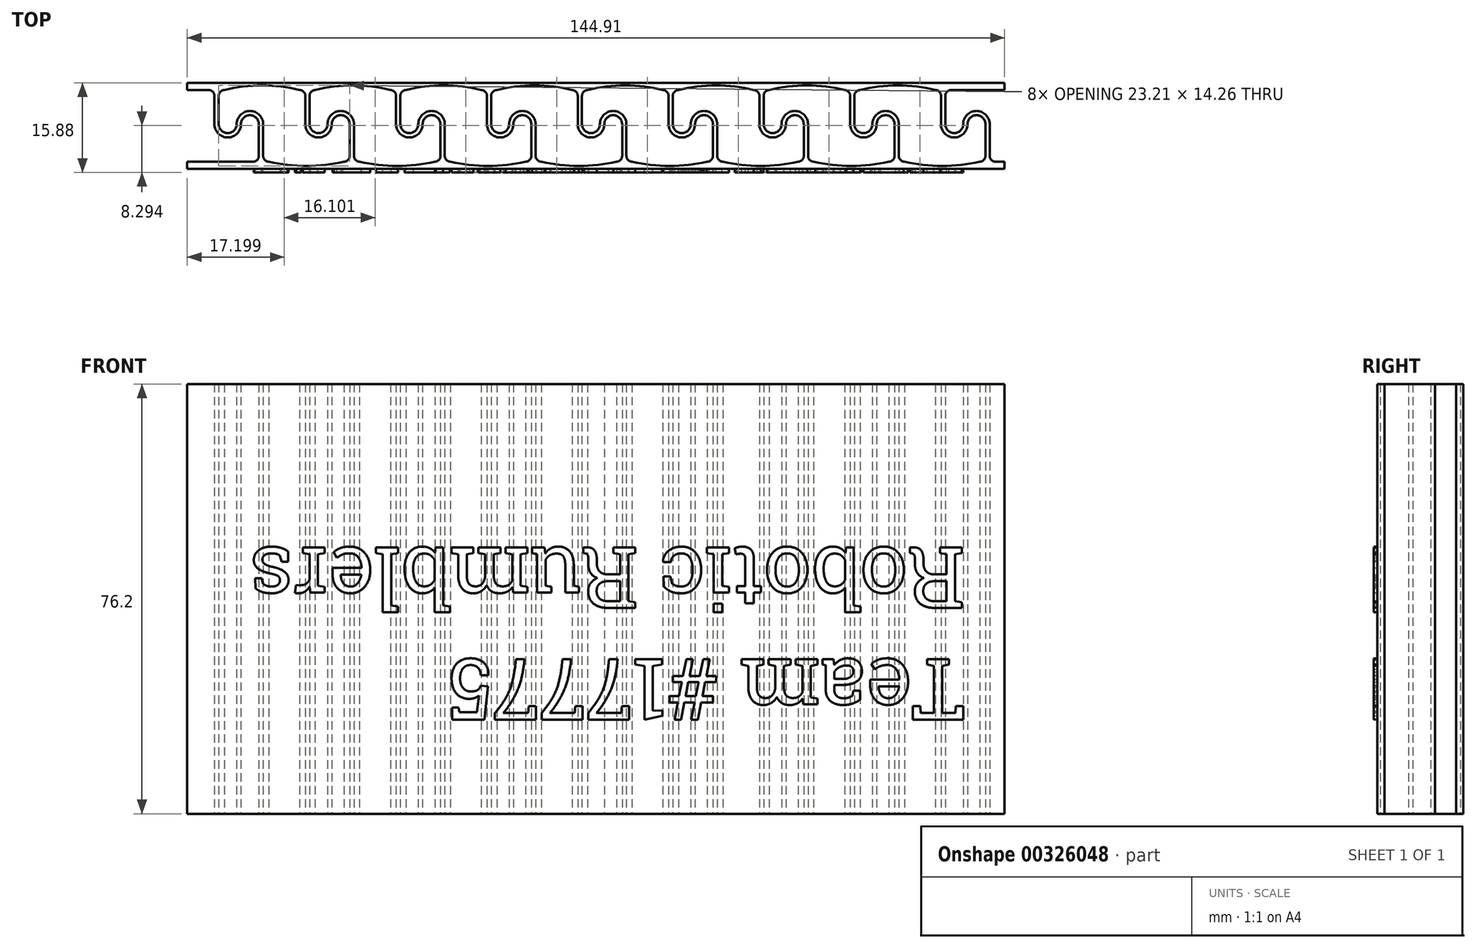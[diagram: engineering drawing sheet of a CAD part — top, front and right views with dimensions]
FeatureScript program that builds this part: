
annotation { "Feature Type Name" : "Feature", "Feature Type Description" : "" }
export const myFeature = defineFeature(function(context is Context, id is Id, definition is map)
    precondition{}
    {
        {
            var Q0;
            Q0=qCreatedBy(makeId("Front.planeOp"),FACE);
            var sketch = newSketch(context, id + "F0", { "sketchPlane" : qUnion([Q0])});
            skLineSegment(sketch, "E0", {"start": v(111.58, -16.44) * mm, "end": v(111.58, -17.71) * mm});
            skLineSegment(sketch, "E1", {"start": v(111.58, -17.71) * mm, "end": v(99.87, -17.71) * mm});
            skLineSegment(sketch, "E2", {"start": v(111.58, -30.41) * mm, "end": v(111.58, -31.68) * mm});
            skLineSegment(sketch, "E3", {"start": v(98.88, -18.7) * mm, "end": v(98.88, -24.35) * mm});
            skArc(sketch, "E4", {"start": v(98.88, -24.35) * mm, "mid": v(100.47, -25.94) * mm, "end": v(102.05, -24.35) * mm});
            skLineSegment(sketch, "E5", {"start": v(98.12, -18.7) * mm, "end": v(98.12, -24.35) * mm});
            skArc(sketch, "E6", {"start": v(98.12, -24.35) * mm, "mid": v(100.47, -26.7) * mm, "end": v(102.82, -24.35) * mm});
            skLineSegment(sketch, "E7", {"start": v(106, -29.42) * mm, "end": v(106, -24.35) * mm});
            skArc(sketch, "E8", {"start": v(106, -24.35) * mm, "mid": v(104.4, -22.77) * mm, "end": v(102.82, -24.35) * mm});
            skLineSegment(sketch, "E9", {"start": v(106.75, -29.42) * mm, "end": v(106.75, -24.35) * mm});
            skArc(sketch, "E10", {"start": v(106.75, -24.35) * mm, "mid": v(104.4, -22) * mm, "end": v(102.05, -24.35) * mm});
            skLineSegment(sketch, "E11", {"start": v(111.58, -30.41) * mm, "end": v(107.75, -30.41) * mm});
            skPoint(sketch, "E12.visualSharp", {"position": v(98.12, -17.71) * mm});
            skArc(sketch, "E12.filletArc", {"start": v(98.12, -18.7) * mm, "mid": v(97.83, -18) * mm, "end": v(97.13, -17.71) * mm});
            skPoint(sketch, "E13.visualSharp", {"position": v(98.88, -17.71) * mm});
            skArc(sketch, "E13.filletArc", {"start": v(99.87, -17.71) * mm, "mid": v(99.17, -18) * mm, "end": v(98.88, -18.7) * mm});
            skPoint(sketch, "E14.visualSharp", {"position": v(106, -30.41) * mm});
            skArc(sketch, "E14.filletArc", {"start": v(105, -30.41) * mm, "mid": v(105.7, -30.12) * mm, "end": v(106, -29.42) * mm});
            skPoint(sketch, "E15.visualSharp", {"position": v(106.75, -30.41) * mm});
            skArc(sketch, "E15.filletArc", {"start": v(106.75, -29.42) * mm, "mid": v(107.04, -30.12) * mm, "end": v(107.75, -30.41) * mm});
            skLineSegment(sketch, "E16", {"start": v(82.78, -18.7) * mm, "end": v(82.78, -24.35) * mm});
            skArc(sketch, "E17", {"start": v(82.78, -24.35) * mm, "mid": v(84.37, -25.94) * mm, "end": v(85.95, -24.35) * mm});
            skLineSegment(sketch, "E18", {"start": v(82.02, -18.7) * mm, "end": v(82.02, -24.35) * mm});
            skArc(sketch, "E19", {"start": v(82.02, -24.35) * mm, "mid": v(84.37, -26.7) * mm, "end": v(86.72, -24.35) * mm});
            skLineSegment(sketch, "E20", {"start": v(89.9, -29.42) * mm, "end": v(89.9, -24.35) * mm});
            skArc(sketch, "E21", {"start": v(89.9, -24.35) * mm, "mid": v(88.3, -22.77) * mm, "end": v(86.72, -24.35) * mm});
            skLineSegment(sketch, "E22", {"start": v(90.65, -29.42) * mm, "end": v(90.65, -24.35) * mm});
            skArc(sketch, "E23", {"start": v(90.65, -24.35) * mm, "mid": v(88.3, -22) * mm, "end": v(85.95, -24.35) * mm});
            skPoint(sketch, "E24.visualSharp", {"position": v(82.02, -17.71) * mm});
            skArc(sketch, "E24.filletArc", {"start": v(82.02, -18.7) * mm, "mid": v(81.73, -18) * mm, "end": v(81.02, -17.71) * mm});
            skPoint(sketch, "E25.visualSharp", {"position": v(82.78, -17.71) * mm});
            skArc(sketch, "E25.filletArc", {"start": v(83.77, -17.71) * mm, "mid": v(83.07, -18) * mm, "end": v(82.78, -18.7) * mm});
            skPoint(sketch, "E26.visualSharp", {"position": v(89.9, -30.41) * mm});
            skArc(sketch, "E26.filletArc", {"start": v(88.9, -30.41) * mm, "mid": v(89.6, -30.12) * mm, "end": v(89.9, -29.42) * mm});
            skPoint(sketch, "E27.visualSharp", {"position": v(90.65, -30.41) * mm});
            skArc(sketch, "E27.filletArc", {"start": v(90.65, -29.42) * mm, "mid": v(90.94, -30.12) * mm, "end": v(91.64, -30.41) * mm});
            skLineSegment(sketch, "E28", {"start": v(78.68, -17.71) * mm, "end": v(67.67, -17.71) * mm});
            skLineSegment(sketch, "E29", {"start": v(66.68, -18.7) * mm, "end": v(66.68, -24.35) * mm});
            skArc(sketch, "E30", {"start": v(66.68, -24.35) * mm, "mid": v(68.27, -25.94) * mm, "end": v(69.85, -24.35) * mm});
            skLineSegment(sketch, "E31", {"start": v(65.92, -18.7) * mm, "end": v(65.92, -24.35) * mm});
            skArc(sketch, "E32", {"start": v(65.92, -24.35) * mm, "mid": v(68.27, -26.7) * mm, "end": v(70.61, -24.35) * mm});
            skLineSegment(sketch, "E33", {"start": v(73.79, -29.42) * mm, "end": v(73.79, -24.35) * mm});
            skArc(sketch, "E34", {"start": v(73.79, -24.35) * mm, "mid": v(72.2, -22.77) * mm, "end": v(70.61, -24.35) * mm});
            skLineSegment(sketch, "E35", {"start": v(74.55, -29.42) * mm, "end": v(74.55, -24.35) * mm});
            skArc(sketch, "E36", {"start": v(74.55, -24.35) * mm, "mid": v(72.2, -22) * mm, "end": v(69.85, -24.35) * mm});
            skPoint(sketch, "E37.visualSharp", {"position": v(65.92, -17.71) * mm});
            skArc(sketch, "E37.filletArc", {"start": v(65.92, -18.7) * mm, "mid": v(65.63, -18) * mm, "end": v(64.92, -17.71) * mm});
            skPoint(sketch, "E38.visualSharp", {"position": v(66.68, -17.71) * mm});
            skArc(sketch, "E38.filletArc", {"start": v(67.67, -17.71) * mm, "mid": v(66.97, -18) * mm, "end": v(66.68, -18.7) * mm});
            skPoint(sketch, "E39.visualSharp", {"position": v(73.79, -30.41) * mm});
            skArc(sketch, "E39.filletArc", {"start": v(72.8, -30.41) * mm, "mid": v(73.5, -30.12) * mm, "end": v(73.79, -29.42) * mm});
            skPoint(sketch, "E40.visualSharp", {"position": v(74.55, -30.41) * mm});
            skArc(sketch, "E40.filletArc", {"start": v(74.55, -29.42) * mm, "mid": v(74.84, -30.12) * mm, "end": v(75.54, -30.41) * mm});
            skLineSegment(sketch, "E41", {"start": v(50.58, -18.7) * mm, "end": v(50.58, -24.35) * mm});
            skArc(sketch, "E42", {"start": v(50.58, -24.35) * mm, "mid": v(52.16, -25.94) * mm, "end": v(53.75, -24.35) * mm});
            skLineSegment(sketch, "E43", {"start": v(49.82, -18.7) * mm, "end": v(49.82, -24.35) * mm});
            skArc(sketch, "E44", {"start": v(49.82, -24.35) * mm, "mid": v(52.16, -26.7) * mm, "end": v(54.51, -24.35) * mm});
            skLineSegment(sketch, "E45", {"start": v(57.69, -29.42) * mm, "end": v(57.69, -24.35) * mm});
            skArc(sketch, "E46", {"start": v(57.69, -24.35) * mm, "mid": v(56.1, -22.77) * mm, "end": v(54.51, -24.35) * mm});
            skLineSegment(sketch, "E47", {"start": v(58.45, -29.42) * mm, "end": v(58.45, -24.35) * mm});
            skArc(sketch, "E48", {"start": v(58.45, -24.35) * mm, "mid": v(56.1, -22) * mm, "end": v(53.75, -24.35) * mm});
            skPoint(sketch, "E49.visualSharp", {"position": v(49.82, -17.71) * mm});
            skArc(sketch, "E49.filletArc", {"start": v(49.82, -18.7) * mm, "mid": v(49.52, -18) * mm, "end": v(48.82, -17.71) * mm});
            skPoint(sketch, "E50.visualSharp", {"position": v(50.58, -17.71) * mm});
            skArc(sketch, "E50.filletArc", {"start": v(51.57, -17.71) * mm, "mid": v(50.87, -18) * mm, "end": v(50.58, -18.7) * mm});
            skPoint(sketch, "E51.visualSharp", {"position": v(57.69, -30.41) * mm});
            skArc(sketch, "E51.filletArc", {"start": v(56.7, -30.41) * mm, "mid": v(57.4, -30.12) * mm, "end": v(57.69, -29.42) * mm});
            skPoint(sketch, "E52.visualSharp", {"position": v(58.45, -30.41) * mm});
            skArc(sketch, "E52.filletArc", {"start": v(58.45, -29.42) * mm, "mid": v(58.74, -30.12) * mm, "end": v(59.44, -30.41) * mm});
            skLineSegment(sketch, "E53", {"start": v(34.48, -18.7) * mm, "end": v(34.48, -24.35) * mm});
            skArc(sketch, "E54", {"start": v(34.48, -24.35) * mm, "mid": v(36.06, -25.94) * mm, "end": v(37.65, -24.35) * mm});
            skLineSegment(sketch, "E55", {"start": v(33.71, -18.7) * mm, "end": v(33.71, -24.35) * mm});
            skArc(sketch, "E56", {"start": v(33.71, -24.35) * mm, "mid": v(36.06, -26.7) * mm, "end": v(38.41, -24.35) * mm});
            skLineSegment(sketch, "E57", {"start": v(41.59, -29.42) * mm, "end": v(41.59, -24.35) * mm});
            skArc(sketch, "E58", {"start": v(41.59, -24.35) * mm, "mid": v(40, -22.77) * mm, "end": v(38.41, -24.35) * mm});
            skLineSegment(sketch, "E59", {"start": v(42.35, -29.42) * mm, "end": v(42.35, -24.35) * mm});
            skArc(sketch, "E60", {"start": v(42.35, -24.35) * mm, "mid": v(40, -22) * mm, "end": v(37.65, -24.35) * mm});
            skPoint(sketch, "E61.visualSharp", {"position": v(33.71, -17.71) * mm});
            skArc(sketch, "E61.filletArc", {"start": v(33.71, -18.7) * mm, "mid": v(33.42, -18) * mm, "end": v(32.72, -17.71) * mm});
            skPoint(sketch, "E62.visualSharp", {"position": v(34.48, -17.71) * mm});
            skArc(sketch, "E62.filletArc", {"start": v(35.47, -17.71) * mm, "mid": v(34.77, -18) * mm, "end": v(34.48, -18.7) * mm});
            skPoint(sketch, "E63.visualSharp", {"position": v(41.59, -30.41) * mm});
            skArc(sketch, "E63.filletArc", {"start": v(40.6, -30.41) * mm, "mid": v(41.3, -30.12) * mm, "end": v(41.59, -29.42) * mm});
            skPoint(sketch, "E64.visualSharp", {"position": v(42.35, -30.41) * mm});
            skArc(sketch, "E64.filletArc", {"start": v(42.35, -29.42) * mm, "mid": v(42.64, -30.12) * mm, "end": v(43.34, -30.41) * mm});
            skLineSegment(sketch, "E65", {"start": v(18.38, -18.7) * mm, "end": v(18.38, -24.35) * mm});
            skArc(sketch, "E66", {"start": v(18.38, -24.35) * mm, "mid": v(19.96, -25.94) * mm, "end": v(21.55, -24.35) * mm});
            skLineSegment(sketch, "E67", {"start": v(17.61, -18.7) * mm, "end": v(17.61, -24.35) * mm});
            skArc(sketch, "E68", {"start": v(17.61, -24.35) * mm, "mid": v(19.96, -26.7) * mm, "end": v(22.31, -24.35) * mm});
            skLineSegment(sketch, "E69", {"start": v(25.49, -29.42) * mm, "end": v(25.49, -24.35) * mm});
            skArc(sketch, "E70", {"start": v(25.49, -24.35) * mm, "mid": v(23.9, -22.77) * mm, "end": v(22.31, -24.35) * mm});
            skLineSegment(sketch, "E71", {"start": v(26.25, -29.42) * mm, "end": v(26.25, -24.35) * mm});
            skArc(sketch, "E72", {"start": v(26.25, -24.35) * mm, "mid": v(23.9, -22) * mm, "end": v(21.55, -24.35) * mm});
            skPoint(sketch, "E73.visualSharp", {"position": v(17.61, -17.71) * mm});
            skArc(sketch, "E73.filletArc", {"start": v(17.61, -18.7) * mm, "mid": v(17.32, -18) * mm, "end": v(16.62, -17.71) * mm});
            skPoint(sketch, "E74.visualSharp", {"position": v(18.38, -17.71) * mm});
            skArc(sketch, "E74.filletArc", {"start": v(19.37, -17.71) * mm, "mid": v(18.67, -18) * mm, "end": v(18.38, -18.7) * mm});
            skPoint(sketch, "E75.visualSharp", {"position": v(25.49, -30.41) * mm});
            skArc(sketch, "E75.filletArc", {"start": v(24.5, -30.41) * mm, "mid": v(25.2, -30.12) * mm, "end": v(25.49, -29.42) * mm});
            skPoint(sketch, "E76.visualSharp", {"position": v(26.25, -30.41) * mm});
            skArc(sketch, "E76.filletArc", {"start": v(26.25, -29.42) * mm, "mid": v(26.54, -30.12) * mm, "end": v(27.24, -30.41) * mm});
            skLineSegment(sketch, "E77", {"start": v(2.27, -18.7) * mm, "end": v(2.27, -24.35) * mm});
            skArc(sketch, "E78", {"start": v(2.27, -24.35) * mm, "mid": v(3.86, -25.94) * mm, "end": v(5.45, -24.35) * mm});
            skLineSegment(sketch, "E79", {"start": v(1.51, -18.7) * mm, "end": v(1.51, -24.35) * mm});
            skArc(sketch, "E80", {"start": v(1.51, -24.35) * mm, "mid": v(3.86, -26.7) * mm, "end": v(6.21, -24.35) * mm});
            skLineSegment(sketch, "E81", {"start": v(9.39, -29.42) * mm, "end": v(9.39, -24.35) * mm});
            skArc(sketch, "E82", {"start": v(9.39, -24.35) * mm, "mid": v(7.8, -22.77) * mm, "end": v(6.21, -24.35) * mm});
            skLineSegment(sketch, "E83", {"start": v(10.15, -29.42) * mm, "end": v(10.15, -24.35) * mm});
            skArc(sketch, "E84", {"start": v(10.15, -24.35) * mm, "mid": v(7.8, -22) * mm, "end": v(5.45, -24.35) * mm});
            skPoint(sketch, "E85.visualSharp", {"position": v(1.51, -17.71) * mm});
            skArc(sketch, "E85.filletArc", {"start": v(1.51, -18.7) * mm, "mid": v(1.22, -18) * mm, "end": v(0.52, -17.71) * mm});
            skPoint(sketch, "E86.visualSharp", {"position": v(2.27, -17.71) * mm});
            skArc(sketch, "E86.filletArc", {"start": v(3.27, -17.71) * mm, "mid": v(2.57, -18) * mm, "end": v(2.27, -18.7) * mm});
            skPoint(sketch, "E87.visualSharp", {"position": v(9.39, -30.41) * mm});
            skArc(sketch, "E87.filletArc", {"start": v(8.4, -30.41) * mm, "mid": v(9.1, -30.12) * mm, "end": v(9.39, -29.42) * mm});
            skPoint(sketch, "E88.visualSharp", {"position": v(10.15, -30.41) * mm});
            skArc(sketch, "E88.filletArc", {"start": v(10.15, -29.42) * mm, "mid": v(10.44, -30.12) * mm, "end": v(11.14, -30.41) * mm});
            skLineSegment(sketch, "E89", {"start": v(-13.83, -18.7) * mm, "end": v(-13.83, -24.35) * mm});
            skArc(sketch, "E90", {"start": v(-13.83, -24.35) * mm, "mid": v(-12.24, -25.94) * mm, "end": v(-10.65, -24.35) * mm});
            skLineSegment(sketch, "E91", {"start": v(-14.59, -18.7) * mm, "end": v(-14.59, -24.35) * mm});
            skArc(sketch, "E92", {"start": v(-14.59, -24.35) * mm, "mid": v(-12.24, -26.7) * mm, "end": v(-9.89, -24.35) * mm});
            skLineSegment(sketch, "E93", {"start": v(-6.71, -29.42) * mm, "end": v(-6.71, -24.35) * mm});
            skArc(sketch, "E94", {"start": v(-6.71, -24.35) * mm, "mid": v(-8.3, -22.77) * mm, "end": v(-9.89, -24.35) * mm});
            skLineSegment(sketch, "E95", {"start": v(-5.95, -29.42) * mm, "end": v(-5.95, -24.35) * mm});
            skArc(sketch, "E96", {"start": v(-5.95, -24.35) * mm, "mid": v(-8.3, -22) * mm, "end": v(-10.65, -24.35) * mm});
            skPoint(sketch, "E97.visualSharp", {"position": v(-14.59, -17.71) * mm});
            skArc(sketch, "E97.filletArc", {"start": v(-14.59, -18.7) * mm, "mid": v(-14.88, -18) * mm, "end": v(-15.58, -17.71) * mm});
            skPoint(sketch, "E98.visualSharp", {"position": v(-13.83, -17.71) * mm});
            skArc(sketch, "E98.filletArc", {"start": v(-12.83, -17.71) * mm, "mid": v(-13.54, -18) * mm, "end": v(-13.83, -18.7) * mm});
            skPoint(sketch, "E99.visualSharp", {"position": v(-6.71, -30.41) * mm});
            skArc(sketch, "E99.filletArc", {"start": v(-7.7, -30.41) * mm, "mid": v(-7, -30.12) * mm, "end": v(-6.71, -29.42) * mm});
            skPoint(sketch, "E100.visualSharp", {"position": v(-5.95, -30.41) * mm});
            skArc(sketch, "E100.filletArc", {"start": v(-5.95, -29.42) * mm, "mid": v(-5.66, -30.12) * mm, "end": v(-4.96, -30.41) * mm});
            skLineSegment(sketch, "E101", {"start": v(-29.93, -18.7) * mm, "end": v(-29.93, -24.35) * mm});
            skArc(sketch, "E102", {"start": v(-29.93, -24.35) * mm, "mid": v(-28.34, -25.94) * mm, "end": v(-26.75, -24.35) * mm});
            skLineSegment(sketch, "E103", {"start": v(-30.69, -18.7) * mm, "end": v(-30.69, -24.35) * mm});
            skArc(sketch, "E104", {"start": v(-30.69, -24.35) * mm, "mid": v(-28.34, -26.7) * mm, "end": v(-25.99, -24.35) * mm});
            skLineSegment(sketch, "E105", {"start": v(-22.81, -29.42) * mm, "end": v(-22.81, -24.35) * mm});
            skArc(sketch, "E106", {"start": v(-22.81, -24.35) * mm, "mid": v(-24.4, -22.77) * mm, "end": v(-25.99, -24.35) * mm});
            skLineSegment(sketch, "E107", {"start": v(-22.05, -29.42) * mm, "end": v(-22.05, -24.35) * mm});
            skArc(sketch, "E108", {"start": v(-22.05, -24.35) * mm, "mid": v(-24.4, -22) * mm, "end": v(-26.75, -24.35) * mm});
            skLineSegment(sketch, "E109", {"start": v(-31.68, -17.71) * mm, "end": v(-33.32, -17.71) * mm});
            skLineSegment(sketch, "E110", {"start": v(-23.8, -30.41) * mm, "end": v(-33.32, -30.41) * mm});
            skPoint(sketch, "E111.visualSharp", {"position": v(-30.69, -17.71) * mm});
            skArc(sketch, "E111.filletArc", {"start": v(-30.69, -18.7) * mm, "mid": v(-30.98, -18) * mm, "end": v(-31.68, -17.71) * mm});
            skPoint(sketch, "E112.visualSharp", {"position": v(-29.93, -17.71) * mm});
            skArc(sketch, "E112.filletArc", {"start": v(-28.93, -17.71) * mm, "mid": v(-29.64, -18) * mm, "end": v(-29.93, -18.7) * mm});
            skPoint(sketch, "E113.visualSharp", {"position": v(-22.81, -30.41) * mm});
            skArc(sketch, "E113.filletArc", {"start": v(-23.8, -30.41) * mm, "mid": v(-23.1, -30.12) * mm, "end": v(-22.81, -29.42) * mm});
            skPoint(sketch, "E114.visualSharp", {"position": v(-22.05, -30.41) * mm});
            skArc(sketch, "E114.filletArc", {"start": v(-22.05, -29.42) * mm, "mid": v(-21.76, -30.12) * mm, "end": v(-21.06, -30.41) * mm});
            skLineSegment(sketch, "E115", {"start": v(111.58, -16.44) * mm, "end": v(-33.32, -16.44) * mm});
            skLineSegment(sketch, "E116", {"start": v(-33.32, -16.44) * mm, "end": v(-33.32, -17.71) * mm});
            skLineSegment(sketch, "E117", {"start": v(111.58, -31.68) * mm, "end": v(-33.32, -31.68) * mm});
            skLineSegment(sketch, "E118", {"start": v(-33.32, -31.68) * mm, "end": v(-33.32, -30.41) * mm});
            skArc(sketch, "E119", {"start": v(-15.58, -17.71) * mm, "mid": v(-22.26, -16.96) * mm, "end": v(-28.93, -17.71) * mm});
            skArc(sketch, "E120", {"start": v(-21.06, -30.41) * mm, "mid": v(-14.38, -31.22) * mm, "end": v(-7.7, -30.41) * mm});
            skArc(sketch, "E121", {"start": v(-4.96, -30.41) * mm, "mid": v(1.72, -31.22) * mm, "end": v(8.4, -30.41) * mm});
            skArc(sketch, "E122", {"start": v(0.52, -17.71) * mm, "mid": v(-6.16, -16.96) * mm, "end": v(-12.83, -17.71) * mm});
            skArc(sketch, "E123", {"start": v(16.62, -17.71) * mm, "mid": v(9.94, -16.96) * mm, "end": v(3.27, -17.71) * mm});
            skArc(sketch, "E124", {"start": v(32.72, -17.71) * mm, "mid": v(26.05, -16.96) * mm, "end": v(19.37, -17.71) * mm});
            skArc(sketch, "E125", {"start": v(11.14, -30.41) * mm, "mid": v(17.82, -31.22) * mm, "end": v(24.5, -30.41) * mm});
            skArc(sketch, "E126", {"start": v(27.24, -30.41) * mm, "mid": v(33.92, -31.22) * mm, "end": v(40.6, -30.41) * mm});
            skArc(sketch, "E127", {"start": v(43.34, -30.41) * mm, "mid": v(50.02, -31.22) * mm, "end": v(56.7, -30.41) * mm});
            skArc(sketch, "E128", {"start": v(59.44, -30.41) * mm, "mid": v(66.12, -31.22) * mm, "end": v(72.8, -30.41) * mm});
            skArc(sketch, "E129", {"start": v(75.54, -30.41) * mm, "mid": v(82.22, -31.22) * mm, "end": v(88.9, -30.41) * mm});
            skArc(sketch, "E130", {"start": v(91.64, -30.41) * mm, "mid": v(98.32, -31.22) * mm, "end": v(105, -30.41) * mm});
            skArc(sketch, "E131", {"start": v(48.82, -17.71) * mm, "mid": v(42.15, -16.96) * mm, "end": v(35.47, -17.71) * mm});
            skArc(sketch, "E132", {"start": v(64.92, -17.71) * mm, "mid": v(58.25, -16.96) * mm, "end": v(51.57, -17.71) * mm});
            skArc(sketch, "E133", {"start": v(81.02, -17.71) * mm, "mid": v(74.35, -16.96) * mm, "end": v(67.67, -17.71) * mm});
            skArc(sketch, "E134", {"start": v(97.13, -17.71) * mm, "mid": v(90.45, -16.96) * mm, "end": v(83.77, -17.71) * mm});
            skSolve(sketch);
        }
        {
            var Q0;
            Q0=makeQuery(id+"F0.imprint","IMPRINT",FACE,{"disambiguationData":[TD([[makeQuery(id+"F0.imprint","IMPRINT",EDGE,{"derivedFrom":sQuery(id+"F0.wireOp",EDGE,"E0")}),-1.0]])]});
            extrude(context, id + "F1", {"entities" : qUnion([Q0]), "depth" : 76.2 * mm});
        }
        {
            var Q0;
            Q0=makeQuery(id+"F1.opExtrude","SWEPT_FACE",FACE,{"disambiguationData":[OSD([sQuery(id+"F0.wireOp",EDGE,"E115")])]});
            var sketch = newSketch(context, id + "F2", { "sketchPlane" : qUnion([Q0])});
            skText(sketch, "E135", { "text": "Team #17775\nRobotic Rumblers\n", "fontName": "RobotoSlab-Regular.ttf"});
            const initialGuessF2  = {"E135": [-0.02624, -0.02738, 1, 0, 0.0108]};
            skSetInitialGuess(sketch, initialGuessF2);
            skSolve(sketch);
        }
        {
            var Q0;
            Q0 = qSketchRegion(id + "F2", true);
            extrude(context, id + "F3", {"entities" : qUnion([Q0]), "operationType" : NewBodyOperationType.ADD, "depth" : 0.64 * mm, "hasDraft" : true, "draftAngle" : 3 * degree});
        }
        {
            var Q0;
            Q0=makeQuery(id+"F1.opExtrude","SWEPT_BODY",BODY,{"disambiguationData":[OSD([sQuery(id+"F0.wireOp",EDGE,"E0"),sQuery(id+"F0.wireOp",EDGE,"E1"),sQuery(id+"F0.wireOp",EDGE,"E2"),sQuery(id+"F0.wireOp",EDGE,"E3"),sQuery(id+"F0.wireOp",EDGE,"E4"),sQuery(id+"F0.wireOp",EDGE,"E5"),sQuery(id+"F0.wireOp",EDGE,"E6"),sQuery(id+"F0.wireOp",EDGE,"E7"),sQuery(id+"F0.wireOp",EDGE,"E8"),sQuery(id+"F0.wireOp",EDGE,"E9"),sQuery(id+"F0.wireOp",EDGE,"E10"),sQuery(id+"F0.wireOp",EDGE,"E11"),sQuery(id+"F0.wireOp",EDGE,"I74NB5Xt-fBUx-Ekq9-JF9C-fknuVL3scMMT"),sQuery(id+"F0.wireOp",EDGE,"4FDFUyAs-k7MS-Wikd-iGz1-CcvRFR4CWyGl"),sQuery(id+"F0.wireOp",EDGE,"E12.filletArc"),sQuery(id+"F0.wireOp",EDGE,"E13.filletArc"),sQuery(id+"F0.wireOp",EDGE,"E14.filletArc"),sQuery(id+"F0.wireOp",EDGE,"E15.filletArc"),sQuery(id+"F0.wireOp",EDGE,"a3bf5448-02e8-47db-9d06-bfbd453e25e5"),sQuery(id+"F0.wireOp",EDGE,"E16"),sQuery(id+"F0.wireOp",EDGE,"E17"),sQuery(id+"F0.wireOp",EDGE,"E18"),sQuery(id+"F0.wireOp",EDGE,"E19"),sQuery(id+"F0.wireOp",EDGE,"E20"),sQuery(id+"F0.wireOp",EDGE,"E21"),sQuery(id+"F0.wireOp",EDGE,"E22"),sQuery(id+"F0.wireOp",EDGE,"E23"),sQuery(id+"F0.wireOp",EDGE,"2c05487f-aafa-4f7c-aa8f-dc711a0f5cb2"),sQuery(id+"F0.wireOp",EDGE,"aa923bbd-f832-4f58-9164-6b3256058c8c"),sQuery(id+"F0.wireOp",EDGE,"d95c7900-678d-4411-9ef4-11f17a881cd2"),sQuery(id+"F0.wireOp",EDGE,"E24.filletArc"),sQuery(id+"F0.wireOp",EDGE,"E25.filletArc"),sQuery(id+"F0.wireOp",EDGE,"E26.filletArc"),sQuery(id+"F0.wireOp",EDGE,"E27.filletArc"),sQuery(id+"F0.wireOp",EDGE,"E28"),sQuery(id+"F0.wireOp",EDGE,"E29"),sQuery(id+"F0.wireOp",EDGE,"E30"),sQuery(id+"F0.wireOp",EDGE,"E31"),sQuery(id+"F0.wireOp",EDGE,"E32"),sQuery(id+"F0.wireOp",EDGE,"E33"),sQuery(id+"F0.wireOp",EDGE,"E34"),sQuery(id+"F0.wireOp",EDGE,"E35"),sQuery(id+"F0.wireOp",EDGE,"E36"),sQuery(id+"F0.wireOp",EDGE,"7487c359-1d13-442e-8d40-6b6f0a60b528"),sQuery(id+"F0.wireOp",EDGE,"0d321a95-f0bf-4603-844a-9d89d9bece21"),sQuery(id+"F0.wireOp",EDGE,"0b63d352-fbcd-48db-a107-9c6472e04aa2"),sQuery(id+"F0.wireOp",EDGE,"E37.filletArc"),sQuery(id+"F0.wireOp",EDGE,"E38.filletArc"),sQuery(id+"F0.wireOp",EDGE,"E39.filletArc"),sQuery(id+"F0.wireOp",EDGE,"E40.filletArc"),sQuery(id+"F0.wireOp",EDGE,"67e7e0cc-1dbd-4a8f-987f-19f6fc1f17c7"),sQuery(id+"F0.wireOp",EDGE,"E41"),sQuery(id+"F0.wireOp",EDGE,"E42"),sQuery(id+"F0.wireOp",EDGE,"E43"),sQuery(id+"F0.wireOp",EDGE,"E44"),sQuery(id+"F0.wireOp",EDGE,"E45"),sQuery(id+"F0.wireOp",EDGE,"E46"),sQuery(id+"F0.wireOp",EDGE,"E47"),sQuery(id+"F0.wireOp",EDGE,"E48"),sQuery(id+"F0.wireOp",EDGE,"d55768ac-2e07-4581-96c8-90a235a94c6e"),sQuery(id+"F0.wireOp",EDGE,"d56cd83a-e035-431e-9127-d553bba9e061"),sQuery(id+"F0.wireOp",EDGE,"8d056239-58ce-4037-b7b6-6b57657910ae"),sQuery(id+"F0.wireOp",EDGE,"E49.filletArc"),sQuery(id+"F0.wireOp",EDGE,"E50.filletArc"),sQuery(id+"F0.wireOp",EDGE,"E51.filletArc"),sQuery(id+"F0.wireOp",EDGE,"E52.filletArc"),sQuery(id+"F0.wireOp",EDGE,"689b71ce-addc-4fa1-bc7e-e4df8c8ebdf9"),sQuery(id+"F0.wireOp",EDGE,"E53"),sQuery(id+"F0.wireOp",EDGE,"E54"),sQuery(id+"F0.wireOp",EDGE,"E55"),sQuery(id+"F0.wireOp",EDGE,"E56"),sQuery(id+"F0.wireOp",EDGE,"E57"),sQuery(id+"F0.wireOp",EDGE,"E58"),sQuery(id+"F0.wireOp",EDGE,"E59"),sQuery(id+"F0.wireOp",EDGE,"E60"),sQuery(id+"F0.wireOp",EDGE,"0f5e8a53-58f9-4088-94ab-621361dd0740"),sQuery(id+"F0.wireOp",EDGE,"c80b85d9-e73a-4eb2-b9b9-34d3dfa9f6f2"),sQuery(id+"F0.wireOp",EDGE,"70b4659f-ba04-44f8-9531-555b2133b5da"),sQuery(id+"F0.wireOp",EDGE,"E61.filletArc"),sQuery(id+"F0.wireOp",EDGE,"E62.filletArc"),sQuery(id+"F0.wireOp",EDGE,"E63.filletArc"),sQuery(id+"F0.wireOp",EDGE,"E64.filletArc"),sQuery(id+"F0.wireOp",EDGE,"30e6c9bc-ddc1-4fb0-937a-8d0deabf5910"),sQuery(id+"F0.wireOp",EDGE,"E65"),sQuery(id+"F0.wireOp",EDGE,"E66"),sQuery(id+"F0.wireOp",EDGE,"E67"),sQuery(id+"F0.wireOp",EDGE,"E68"),sQuery(id+"F0.wireOp",EDGE,"E69"),sQuery(id+"F0.wireOp",EDGE,"E70"),sQuery(id+"F0.wireOp",EDGE,"E71"),sQuery(id+"F0.wireOp",EDGE,"E72"),sQuery(id+"F0.wireOp",EDGE,"8f9fa5c3-c251-432c-b5cf-c271094e8503"),sQuery(id+"F0.wireOp",EDGE,"48fe9f69-4303-4a16-b855-5b18747e6bbd"),sQuery(id+"F0.wireOp",EDGE,"adddb319-75e6-4134-aa0c-543cc49d29cf"),sQuery(id+"F0.wireOp",EDGE,"E73.filletArc"),sQuery(id+"F0.wireOp",EDGE,"E74.filletArc"),sQuery(id+"F0.wireOp",EDGE,"E75.filletArc"),sQuery(id+"F0.wireOp",EDGE,"E76.filletArc"),sQuery(id+"F0.wireOp",EDGE,"794929a8-fd93-45ab-9b8a-a8aae1a8e309"),sQuery(id+"F0.wireOp",EDGE,"E77"),sQuery(id+"F0.wireOp",EDGE,"E78"),sQuery(id+"F0.wireOp",EDGE,"E79"),sQuery(id+"F0.wireOp",EDGE,"E80"),sQuery(id+"F0.wireOp",EDGE,"E81"),sQuery(id+"F0.wireOp",EDGE,"E82"),sQuery(id+"F0.wireOp",EDGE,"E83"),sQuery(id+"F0.wireOp",EDGE,"E84"),sQuery(id+"F0.wireOp",EDGE,"c2507384-40c0-4369-9541-7014aa20dc06"),sQuery(id+"F0.wireOp",EDGE,"1daf244b-b26d-4da6-aa17-2b1b48277eff"),sQuery(id+"F0.wireOp",EDGE,"f3f5064b-9514-43f3-86fe-7d8dfe96d7c0"),sQuery(id+"F0.wireOp",EDGE,"E85.filletArc"),sQuery(id+"F0.wireOp",EDGE,"E86.filletArc"),sQuery(id+"F0.wireOp",EDGE,"E87.filletArc"),sQuery(id+"F0.wireOp",EDGE,"E88.filletArc"),sQuery(id+"F0.wireOp",EDGE,"db05fb30-ff1c-46d8-ad61-f310132a52e9"),sQuery(id+"F0.wireOp",EDGE,"E89"),sQuery(id+"F0.wireOp",EDGE,"E90"),sQuery(id+"F0.wireOp",EDGE,"E91"),sQuery(id+"F0.wireOp",EDGE,"E92"),sQuery(id+"F0.wireOp",EDGE,"E93"),sQuery(id+"F0.wireOp",EDGE,"E94"),sQuery(id+"F0.wireOp",EDGE,"E95"),sQuery(id+"F0.wireOp",EDGE,"E96"),sQuery(id+"F0.wireOp",EDGE,"1130a4e5-352a-40db-811d-9c2f480c6459"),sQuery(id+"F0.wireOp",EDGE,"eab22e00-a051-4c91-887e-3bb937c10980"),sQuery(id+"F0.wireOp",EDGE,"d1e682f2-d9a5-40f1-908d-0a2fb979e1ca"),sQuery(id+"F0.wireOp",EDGE,"E97.filletArc"),sQuery(id+"F0.wireOp",EDGE,"E98.filletArc"),sQuery(id+"F0.wireOp",EDGE,"E99.filletArc"),sQuery(id+"F0.wireOp",EDGE,"E100.filletArc"),sQuery(id+"F0.wireOp",EDGE,"e89af864-c7d1-4349-afac-df63decef93c"),sQuery(id+"F0.wireOp",EDGE,"E101"),sQuery(id+"F0.wireOp",EDGE,"E102"),sQuery(id+"F0.wireOp",EDGE,"E103"),sQuery(id+"F0.wireOp",EDGE,"E104"),sQuery(id+"F0.wireOp",EDGE,"E105"),sQuery(id+"F0.wireOp",EDGE,"E106"),sQuery(id+"F0.wireOp",EDGE,"E107"),sQuery(id+"F0.wireOp",EDGE,"E108"),sQuery(id+"F0.wireOp",EDGE,"23fffc08-2727-465d-9e6f-753851ddf39a"),sQuery(id+"F0.wireOp",EDGE,"E109"),sQuery(id+"F0.wireOp",EDGE,"E110"),sQuery(id+"F0.wireOp",EDGE,"E111.filletArc"),sQuery(id+"F0.wireOp",EDGE,"E112.filletArc"),sQuery(id+"F0.wireOp",EDGE,"E113.filletArc"),sQuery(id+"F0.wireOp",EDGE,"E114.filletArc"),sQuery(id+"F0.wireOp",EDGE,"E115"),sQuery(id+"F0.wireOp",EDGE,"E116"),sQuery(id+"F0.wireOp",EDGE,"E117"),sQuery(id+"F0.wireOp",EDGE,"E118")])]});
            var Q1;
            Q1=makeQuery(id+"F1.opExtrude","CAP_VERTEX",VERTEX,{"disambiguationData":[OSD([sQuery(id+"F0.wireOp",EDGE,"E117"),sQuery(id+"F0.wireOp",EDGE,"E118")])],"isStart":true});
            var Q2;
            Q2=qCreatedBy(makeId("Origin.pointOp"),VERTEX);
            transform(context, id + "F4", {"entities" : qUnion([Q0]), "transformType" : TransformType.TRANSLATION_ENTITY, "oppositeDirectionEntity" : false, "transformLine" : qUnion([Q1, Q2]), "makeCopy" : false});
        }
        {
            var Q0;
            Q0=makeQuery(id+"F1.opExtrude","SWEPT_BODY",BODY,{"disambiguationData":[OSD([sQuery(id+"F0.wireOp",EDGE,"E0"),sQuery(id+"F0.wireOp",EDGE,"E1"),sQuery(id+"F0.wireOp",EDGE,"E2"),sQuery(id+"F0.wireOp",EDGE,"E3"),sQuery(id+"F0.wireOp",EDGE,"E4"),sQuery(id+"F0.wireOp",EDGE,"E5"),sQuery(id+"F0.wireOp",EDGE,"E6"),sQuery(id+"F0.wireOp",EDGE,"E7"),sQuery(id+"F0.wireOp",EDGE,"E8"),sQuery(id+"F0.wireOp",EDGE,"E9"),sQuery(id+"F0.wireOp",EDGE,"E10"),sQuery(id+"F0.wireOp",EDGE,"E11"),sQuery(id+"F0.wireOp",EDGE,"I74NB5Xt-fBUx-Ekq9-JF9C-fknuVL3scMMT"),sQuery(id+"F0.wireOp",EDGE,"4FDFUyAs-k7MS-Wikd-iGz1-CcvRFR4CWyGl"),sQuery(id+"F0.wireOp",EDGE,"E12.filletArc"),sQuery(id+"F0.wireOp",EDGE,"E13.filletArc"),sQuery(id+"F0.wireOp",EDGE,"E14.filletArc"),sQuery(id+"F0.wireOp",EDGE,"E15.filletArc"),sQuery(id+"F0.wireOp",EDGE,"a3bf5448-02e8-47db-9d06-bfbd453e25e5"),sQuery(id+"F0.wireOp",EDGE,"E16"),sQuery(id+"F0.wireOp",EDGE,"E17"),sQuery(id+"F0.wireOp",EDGE,"E18"),sQuery(id+"F0.wireOp",EDGE,"E19"),sQuery(id+"F0.wireOp",EDGE,"E20"),sQuery(id+"F0.wireOp",EDGE,"E21"),sQuery(id+"F0.wireOp",EDGE,"E22"),sQuery(id+"F0.wireOp",EDGE,"E23"),sQuery(id+"F0.wireOp",EDGE,"2c05487f-aafa-4f7c-aa8f-dc711a0f5cb2"),sQuery(id+"F0.wireOp",EDGE,"aa923bbd-f832-4f58-9164-6b3256058c8c"),sQuery(id+"F0.wireOp",EDGE,"d95c7900-678d-4411-9ef4-11f17a881cd2"),sQuery(id+"F0.wireOp",EDGE,"E24.filletArc"),sQuery(id+"F0.wireOp",EDGE,"E25.filletArc"),sQuery(id+"F0.wireOp",EDGE,"E26.filletArc"),sQuery(id+"F0.wireOp",EDGE,"E27.filletArc"),sQuery(id+"F0.wireOp",EDGE,"E28"),sQuery(id+"F0.wireOp",EDGE,"E29"),sQuery(id+"F0.wireOp",EDGE,"E30"),sQuery(id+"F0.wireOp",EDGE,"E31"),sQuery(id+"F0.wireOp",EDGE,"E32"),sQuery(id+"F0.wireOp",EDGE,"E33"),sQuery(id+"F0.wireOp",EDGE,"E34"),sQuery(id+"F0.wireOp",EDGE,"E35"),sQuery(id+"F0.wireOp",EDGE,"E36"),sQuery(id+"F0.wireOp",EDGE,"7487c359-1d13-442e-8d40-6b6f0a60b528"),sQuery(id+"F0.wireOp",EDGE,"0d321a95-f0bf-4603-844a-9d89d9bece21"),sQuery(id+"F0.wireOp",EDGE,"0b63d352-fbcd-48db-a107-9c6472e04aa2"),sQuery(id+"F0.wireOp",EDGE,"E37.filletArc"),sQuery(id+"F0.wireOp",EDGE,"E38.filletArc"),sQuery(id+"F0.wireOp",EDGE,"E39.filletArc"),sQuery(id+"F0.wireOp",EDGE,"E40.filletArc"),sQuery(id+"F0.wireOp",EDGE,"67e7e0cc-1dbd-4a8f-987f-19f6fc1f17c7"),sQuery(id+"F0.wireOp",EDGE,"E41"),sQuery(id+"F0.wireOp",EDGE,"E42"),sQuery(id+"F0.wireOp",EDGE,"E43"),sQuery(id+"F0.wireOp",EDGE,"E44"),sQuery(id+"F0.wireOp",EDGE,"E45"),sQuery(id+"F0.wireOp",EDGE,"E46"),sQuery(id+"F0.wireOp",EDGE,"E47"),sQuery(id+"F0.wireOp",EDGE,"E48"),sQuery(id+"F0.wireOp",EDGE,"d55768ac-2e07-4581-96c8-90a235a94c6e"),sQuery(id+"F0.wireOp",EDGE,"d56cd83a-e035-431e-9127-d553bba9e061"),sQuery(id+"F0.wireOp",EDGE,"8d056239-58ce-4037-b7b6-6b57657910ae"),sQuery(id+"F0.wireOp",EDGE,"E49.filletArc"),sQuery(id+"F0.wireOp",EDGE,"E50.filletArc"),sQuery(id+"F0.wireOp",EDGE,"E51.filletArc"),sQuery(id+"F0.wireOp",EDGE,"E52.filletArc"),sQuery(id+"F0.wireOp",EDGE,"689b71ce-addc-4fa1-bc7e-e4df8c8ebdf9"),sQuery(id+"F0.wireOp",EDGE,"E53"),sQuery(id+"F0.wireOp",EDGE,"E54"),sQuery(id+"F0.wireOp",EDGE,"E55"),sQuery(id+"F0.wireOp",EDGE,"E56"),sQuery(id+"F0.wireOp",EDGE,"E57"),sQuery(id+"F0.wireOp",EDGE,"E58"),sQuery(id+"F0.wireOp",EDGE,"E59"),sQuery(id+"F0.wireOp",EDGE,"E60"),sQuery(id+"F0.wireOp",EDGE,"0f5e8a53-58f9-4088-94ab-621361dd0740"),sQuery(id+"F0.wireOp",EDGE,"c80b85d9-e73a-4eb2-b9b9-34d3dfa9f6f2"),sQuery(id+"F0.wireOp",EDGE,"70b4659f-ba04-44f8-9531-555b2133b5da"),sQuery(id+"F0.wireOp",EDGE,"E61.filletArc"),sQuery(id+"F0.wireOp",EDGE,"E62.filletArc"),sQuery(id+"F0.wireOp",EDGE,"E63.filletArc"),sQuery(id+"F0.wireOp",EDGE,"E64.filletArc"),sQuery(id+"F0.wireOp",EDGE,"30e6c9bc-ddc1-4fb0-937a-8d0deabf5910"),sQuery(id+"F0.wireOp",EDGE,"E65"),sQuery(id+"F0.wireOp",EDGE,"E66"),sQuery(id+"F0.wireOp",EDGE,"E67"),sQuery(id+"F0.wireOp",EDGE,"E68"),sQuery(id+"F0.wireOp",EDGE,"E69"),sQuery(id+"F0.wireOp",EDGE,"E70"),sQuery(id+"F0.wireOp",EDGE,"E71"),sQuery(id+"F0.wireOp",EDGE,"E72"),sQuery(id+"F0.wireOp",EDGE,"8f9fa5c3-c251-432c-b5cf-c271094e8503"),sQuery(id+"F0.wireOp",EDGE,"48fe9f69-4303-4a16-b855-5b18747e6bbd"),sQuery(id+"F0.wireOp",EDGE,"adddb319-75e6-4134-aa0c-543cc49d29cf"),sQuery(id+"F0.wireOp",EDGE,"E73.filletArc"),sQuery(id+"F0.wireOp",EDGE,"E74.filletArc"),sQuery(id+"F0.wireOp",EDGE,"E75.filletArc"),sQuery(id+"F0.wireOp",EDGE,"E76.filletArc"),sQuery(id+"F0.wireOp",EDGE,"794929a8-fd93-45ab-9b8a-a8aae1a8e309"),sQuery(id+"F0.wireOp",EDGE,"E77"),sQuery(id+"F0.wireOp",EDGE,"E78"),sQuery(id+"F0.wireOp",EDGE,"E79"),sQuery(id+"F0.wireOp",EDGE,"E80"),sQuery(id+"F0.wireOp",EDGE,"E81"),sQuery(id+"F0.wireOp",EDGE,"E82"),sQuery(id+"F0.wireOp",EDGE,"E83"),sQuery(id+"F0.wireOp",EDGE,"E84"),sQuery(id+"F0.wireOp",EDGE,"c2507384-40c0-4369-9541-7014aa20dc06"),sQuery(id+"F0.wireOp",EDGE,"1daf244b-b26d-4da6-aa17-2b1b48277eff"),sQuery(id+"F0.wireOp",EDGE,"f3f5064b-9514-43f3-86fe-7d8dfe96d7c0"),sQuery(id+"F0.wireOp",EDGE,"E85.filletArc"),sQuery(id+"F0.wireOp",EDGE,"E86.filletArc"),sQuery(id+"F0.wireOp",EDGE,"E87.filletArc"),sQuery(id+"F0.wireOp",EDGE,"E88.filletArc"),sQuery(id+"F0.wireOp",EDGE,"db05fb30-ff1c-46d8-ad61-f310132a52e9"),sQuery(id+"F0.wireOp",EDGE,"E89"),sQuery(id+"F0.wireOp",EDGE,"E90"),sQuery(id+"F0.wireOp",EDGE,"E91"),sQuery(id+"F0.wireOp",EDGE,"E92"),sQuery(id+"F0.wireOp",EDGE,"E93"),sQuery(id+"F0.wireOp",EDGE,"E94"),sQuery(id+"F0.wireOp",EDGE,"E95"),sQuery(id+"F0.wireOp",EDGE,"E96"),sQuery(id+"F0.wireOp",EDGE,"1130a4e5-352a-40db-811d-9c2f480c6459"),sQuery(id+"F0.wireOp",EDGE,"eab22e00-a051-4c91-887e-3bb937c10980"),sQuery(id+"F0.wireOp",EDGE,"d1e682f2-d9a5-40f1-908d-0a2fb979e1ca"),sQuery(id+"F0.wireOp",EDGE,"E97.filletArc"),sQuery(id+"F0.wireOp",EDGE,"E98.filletArc"),sQuery(id+"F0.wireOp",EDGE,"E99.filletArc"),sQuery(id+"F0.wireOp",EDGE,"E100.filletArc"),sQuery(id+"F0.wireOp",EDGE,"e89af864-c7d1-4349-afac-df63decef93c"),sQuery(id+"F0.wireOp",EDGE,"E101"),sQuery(id+"F0.wireOp",EDGE,"E102"),sQuery(id+"F0.wireOp",EDGE,"E103"),sQuery(id+"F0.wireOp",EDGE,"E104"),sQuery(id+"F0.wireOp",EDGE,"E105"),sQuery(id+"F0.wireOp",EDGE,"E106"),sQuery(id+"F0.wireOp",EDGE,"E107"),sQuery(id+"F0.wireOp",EDGE,"E108"),sQuery(id+"F0.wireOp",EDGE,"23fffc08-2727-465d-9e6f-753851ddf39a"),sQuery(id+"F0.wireOp",EDGE,"E109"),sQuery(id+"F0.wireOp",EDGE,"E110"),sQuery(id+"F0.wireOp",EDGE,"E111.filletArc"),sQuery(id+"F0.wireOp",EDGE,"E112.filletArc"),sQuery(id+"F0.wireOp",EDGE,"E113.filletArc"),sQuery(id+"F0.wireOp",EDGE,"E114.filletArc"),sQuery(id+"F0.wireOp",EDGE,"E115"),sQuery(id+"F0.wireOp",EDGE,"E116"),sQuery(id+"F0.wireOp",EDGE,"E117"),sQuery(id+"F0.wireOp",EDGE,"E118")])]});
            var Q1;
            Q1=makeQuery(id+"F1.opExtrude","CAP_EDGE",EDGE,{"disambiguationData":[OSD([sQuery(id+"F0.wireOp",EDGE,"E117")])],"isStart":true});
            transform(context, id + "F5", {"entities" : qUnion([Q0]), "transformType" : TransformType.ROTATION, "transformAxis" : qUnion([Q1]), "angle" : 90 * degree, "makeCopy" : false});
        }
        {
            var Q0;
            Q0=makeQuery(id+"F1.opExtrude","SWEPT_BODY",BODY,{"disambiguationData":[OSD([sQuery(id+"F0.wireOp",EDGE,"E0"),sQuery(id+"F0.wireOp",EDGE,"E1"),sQuery(id+"F0.wireOp",EDGE,"E2"),sQuery(id+"F0.wireOp",EDGE,"E3"),sQuery(id+"F0.wireOp",EDGE,"E4"),sQuery(id+"F0.wireOp",EDGE,"E5"),sQuery(id+"F0.wireOp",EDGE,"E6"),sQuery(id+"F0.wireOp",EDGE,"E7"),sQuery(id+"F0.wireOp",EDGE,"E8"),sQuery(id+"F0.wireOp",EDGE,"E9"),sQuery(id+"F0.wireOp",EDGE,"E10"),sQuery(id+"F0.wireOp",EDGE,"E11"),sQuery(id+"F0.wireOp",EDGE,"I74NB5Xt-fBUx-Ekq9-JF9C-fknuVL3scMMT"),sQuery(id+"F0.wireOp",EDGE,"4FDFUyAs-k7MS-Wikd-iGz1-CcvRFR4CWyGl"),sQuery(id+"F0.wireOp",EDGE,"E12.filletArc"),sQuery(id+"F0.wireOp",EDGE,"E13.filletArc"),sQuery(id+"F0.wireOp",EDGE,"E14.filletArc"),sQuery(id+"F0.wireOp",EDGE,"E15.filletArc"),sQuery(id+"F0.wireOp",EDGE,"a3bf5448-02e8-47db-9d06-bfbd453e25e5"),sQuery(id+"F0.wireOp",EDGE,"E16"),sQuery(id+"F0.wireOp",EDGE,"E17"),sQuery(id+"F0.wireOp",EDGE,"E18"),sQuery(id+"F0.wireOp",EDGE,"E19"),sQuery(id+"F0.wireOp",EDGE,"E20"),sQuery(id+"F0.wireOp",EDGE,"E21"),sQuery(id+"F0.wireOp",EDGE,"E22"),sQuery(id+"F0.wireOp",EDGE,"E23"),sQuery(id+"F0.wireOp",EDGE,"2c05487f-aafa-4f7c-aa8f-dc711a0f5cb2"),sQuery(id+"F0.wireOp",EDGE,"aa923bbd-f832-4f58-9164-6b3256058c8c"),sQuery(id+"F0.wireOp",EDGE,"d95c7900-678d-4411-9ef4-11f17a881cd2"),sQuery(id+"F0.wireOp",EDGE,"E24.filletArc"),sQuery(id+"F0.wireOp",EDGE,"E25.filletArc"),sQuery(id+"F0.wireOp",EDGE,"E26.filletArc"),sQuery(id+"F0.wireOp",EDGE,"E27.filletArc"),sQuery(id+"F0.wireOp",EDGE,"E28"),sQuery(id+"F0.wireOp",EDGE,"E29"),sQuery(id+"F0.wireOp",EDGE,"E30"),sQuery(id+"F0.wireOp",EDGE,"E31"),sQuery(id+"F0.wireOp",EDGE,"E32"),sQuery(id+"F0.wireOp",EDGE,"E33"),sQuery(id+"F0.wireOp",EDGE,"E34"),sQuery(id+"F0.wireOp",EDGE,"E35"),sQuery(id+"F0.wireOp",EDGE,"E36"),sQuery(id+"F0.wireOp",EDGE,"7487c359-1d13-442e-8d40-6b6f0a60b528"),sQuery(id+"F0.wireOp",EDGE,"0d321a95-f0bf-4603-844a-9d89d9bece21"),sQuery(id+"F0.wireOp",EDGE,"0b63d352-fbcd-48db-a107-9c6472e04aa2"),sQuery(id+"F0.wireOp",EDGE,"E37.filletArc"),sQuery(id+"F0.wireOp",EDGE,"E38.filletArc"),sQuery(id+"F0.wireOp",EDGE,"E39.filletArc"),sQuery(id+"F0.wireOp",EDGE,"E40.filletArc"),sQuery(id+"F0.wireOp",EDGE,"67e7e0cc-1dbd-4a8f-987f-19f6fc1f17c7"),sQuery(id+"F0.wireOp",EDGE,"E41"),sQuery(id+"F0.wireOp",EDGE,"E42"),sQuery(id+"F0.wireOp",EDGE,"E43"),sQuery(id+"F0.wireOp",EDGE,"E44"),sQuery(id+"F0.wireOp",EDGE,"E45"),sQuery(id+"F0.wireOp",EDGE,"E46"),sQuery(id+"F0.wireOp",EDGE,"E47"),sQuery(id+"F0.wireOp",EDGE,"E48"),sQuery(id+"F0.wireOp",EDGE,"d55768ac-2e07-4581-96c8-90a235a94c6e"),sQuery(id+"F0.wireOp",EDGE,"d56cd83a-e035-431e-9127-d553bba9e061"),sQuery(id+"F0.wireOp",EDGE,"8d056239-58ce-4037-b7b6-6b57657910ae"),sQuery(id+"F0.wireOp",EDGE,"E49.filletArc"),sQuery(id+"F0.wireOp",EDGE,"E50.filletArc"),sQuery(id+"F0.wireOp",EDGE,"E51.filletArc"),sQuery(id+"F0.wireOp",EDGE,"E52.filletArc"),sQuery(id+"F0.wireOp",EDGE,"689b71ce-addc-4fa1-bc7e-e4df8c8ebdf9"),sQuery(id+"F0.wireOp",EDGE,"E53"),sQuery(id+"F0.wireOp",EDGE,"E54"),sQuery(id+"F0.wireOp",EDGE,"E55"),sQuery(id+"F0.wireOp",EDGE,"E56"),sQuery(id+"F0.wireOp",EDGE,"E57"),sQuery(id+"F0.wireOp",EDGE,"E58"),sQuery(id+"F0.wireOp",EDGE,"E59"),sQuery(id+"F0.wireOp",EDGE,"E60"),sQuery(id+"F0.wireOp",EDGE,"0f5e8a53-58f9-4088-94ab-621361dd0740"),sQuery(id+"F0.wireOp",EDGE,"c80b85d9-e73a-4eb2-b9b9-34d3dfa9f6f2"),sQuery(id+"F0.wireOp",EDGE,"70b4659f-ba04-44f8-9531-555b2133b5da"),sQuery(id+"F0.wireOp",EDGE,"E61.filletArc"),sQuery(id+"F0.wireOp",EDGE,"E62.filletArc"),sQuery(id+"F0.wireOp",EDGE,"E63.filletArc"),sQuery(id+"F0.wireOp",EDGE,"E64.filletArc"),sQuery(id+"F0.wireOp",EDGE,"30e6c9bc-ddc1-4fb0-937a-8d0deabf5910"),sQuery(id+"F0.wireOp",EDGE,"E65"),sQuery(id+"F0.wireOp",EDGE,"E66"),sQuery(id+"F0.wireOp",EDGE,"E67"),sQuery(id+"F0.wireOp",EDGE,"E68"),sQuery(id+"F0.wireOp",EDGE,"E69"),sQuery(id+"F0.wireOp",EDGE,"E70"),sQuery(id+"F0.wireOp",EDGE,"E71"),sQuery(id+"F0.wireOp",EDGE,"E72"),sQuery(id+"F0.wireOp",EDGE,"8f9fa5c3-c251-432c-b5cf-c271094e8503"),sQuery(id+"F0.wireOp",EDGE,"48fe9f69-4303-4a16-b855-5b18747e6bbd"),sQuery(id+"F0.wireOp",EDGE,"adddb319-75e6-4134-aa0c-543cc49d29cf"),sQuery(id+"F0.wireOp",EDGE,"E73.filletArc"),sQuery(id+"F0.wireOp",EDGE,"E74.filletArc"),sQuery(id+"F0.wireOp",EDGE,"E75.filletArc"),sQuery(id+"F0.wireOp",EDGE,"E76.filletArc"),sQuery(id+"F0.wireOp",EDGE,"794929a8-fd93-45ab-9b8a-a8aae1a8e309"),sQuery(id+"F0.wireOp",EDGE,"E77"),sQuery(id+"F0.wireOp",EDGE,"E78"),sQuery(id+"F0.wireOp",EDGE,"E79"),sQuery(id+"F0.wireOp",EDGE,"E80"),sQuery(id+"F0.wireOp",EDGE,"E81"),sQuery(id+"F0.wireOp",EDGE,"E82"),sQuery(id+"F0.wireOp",EDGE,"E83"),sQuery(id+"F0.wireOp",EDGE,"E84"),sQuery(id+"F0.wireOp",EDGE,"c2507384-40c0-4369-9541-7014aa20dc06"),sQuery(id+"F0.wireOp",EDGE,"1daf244b-b26d-4da6-aa17-2b1b48277eff"),sQuery(id+"F0.wireOp",EDGE,"f3f5064b-9514-43f3-86fe-7d8dfe96d7c0"),sQuery(id+"F0.wireOp",EDGE,"E85.filletArc"),sQuery(id+"F0.wireOp",EDGE,"E86.filletArc"),sQuery(id+"F0.wireOp",EDGE,"E87.filletArc"),sQuery(id+"F0.wireOp",EDGE,"E88.filletArc"),sQuery(id+"F0.wireOp",EDGE,"db05fb30-ff1c-46d8-ad61-f310132a52e9"),sQuery(id+"F0.wireOp",EDGE,"E89"),sQuery(id+"F0.wireOp",EDGE,"E90"),sQuery(id+"F0.wireOp",EDGE,"E91"),sQuery(id+"F0.wireOp",EDGE,"E92"),sQuery(id+"F0.wireOp",EDGE,"E93"),sQuery(id+"F0.wireOp",EDGE,"E94"),sQuery(id+"F0.wireOp",EDGE,"E95"),sQuery(id+"F0.wireOp",EDGE,"E96"),sQuery(id+"F0.wireOp",EDGE,"1130a4e5-352a-40db-811d-9c2f480c6459"),sQuery(id+"F0.wireOp",EDGE,"eab22e00-a051-4c91-887e-3bb937c10980"),sQuery(id+"F0.wireOp",EDGE,"d1e682f2-d9a5-40f1-908d-0a2fb979e1ca"),sQuery(id+"F0.wireOp",EDGE,"E97.filletArc"),sQuery(id+"F0.wireOp",EDGE,"E98.filletArc"),sQuery(id+"F0.wireOp",EDGE,"E99.filletArc"),sQuery(id+"F0.wireOp",EDGE,"E100.filletArc"),sQuery(id+"F0.wireOp",EDGE,"e89af864-c7d1-4349-afac-df63decef93c"),sQuery(id+"F0.wireOp",EDGE,"E101"),sQuery(id+"F0.wireOp",EDGE,"E102"),sQuery(id+"F0.wireOp",EDGE,"E103"),sQuery(id+"F0.wireOp",EDGE,"E104"),sQuery(id+"F0.wireOp",EDGE,"E105"),sQuery(id+"F0.wireOp",EDGE,"E106"),sQuery(id+"F0.wireOp",EDGE,"E107"),sQuery(id+"F0.wireOp",EDGE,"E108"),sQuery(id+"F0.wireOp",EDGE,"23fffc08-2727-465d-9e6f-753851ddf39a"),sQuery(id+"F0.wireOp",EDGE,"E109"),sQuery(id+"F0.wireOp",EDGE,"E110"),sQuery(id+"F0.wireOp",EDGE,"E111.filletArc"),sQuery(id+"F0.wireOp",EDGE,"E112.filletArc"),sQuery(id+"F0.wireOp",EDGE,"E113.filletArc"),sQuery(id+"F0.wireOp",EDGE,"E114.filletArc"),sQuery(id+"F0.wireOp",EDGE,"E115"),sQuery(id+"F0.wireOp",EDGE,"E116"),sQuery(id+"F0.wireOp",EDGE,"E117"),sQuery(id+"F0.wireOp",EDGE,"E118")])]});
            var Q1;
            Q1=makeQuery(id+"F1.opExtrude","SWEPT_EDGE",EDGE,{"disambiguationData":[OSD([sQuery(id+"F0.wireOp",EDGE,"E117"),sQuery(id+"F0.wireOp",EDGE,"E118")])]});
            transform(context, id + "F6", {"entities" : qUnion([Q0]), "transformType" : TransformType.ROTATION, "transformAxis" : qUnion([Q1]), "angle" : 180 * degree, "makeCopy" : false});
        }
        {
            var Q0;
            Q0=makeQuery(id+"F1.opExtrude","SWEPT_BODY",BODY,{"disambiguationData":[OSD([sQuery(id+"F0.wireOp",EDGE,"E0"),sQuery(id+"F0.wireOp",EDGE,"E1"),sQuery(id+"F0.wireOp",EDGE,"E2"),sQuery(id+"F0.wireOp",EDGE,"E3"),sQuery(id+"F0.wireOp",EDGE,"E4"),sQuery(id+"F0.wireOp",EDGE,"E5"),sQuery(id+"F0.wireOp",EDGE,"E6"),sQuery(id+"F0.wireOp",EDGE,"E7"),sQuery(id+"F0.wireOp",EDGE,"E8"),sQuery(id+"F0.wireOp",EDGE,"E9"),sQuery(id+"F0.wireOp",EDGE,"E10"),sQuery(id+"F0.wireOp",EDGE,"E11"),sQuery(id+"F0.wireOp",EDGE,"I74NB5Xt-fBUx-Ekq9-JF9C-fknuVL3scMMT"),sQuery(id+"F0.wireOp",EDGE,"4FDFUyAs-k7MS-Wikd-iGz1-CcvRFR4CWyGl"),sQuery(id+"F0.wireOp",EDGE,"E12.filletArc"),sQuery(id+"F0.wireOp",EDGE,"E13.filletArc"),sQuery(id+"F0.wireOp",EDGE,"E14.filletArc"),sQuery(id+"F0.wireOp",EDGE,"E15.filletArc"),sQuery(id+"F0.wireOp",EDGE,"a3bf5448-02e8-47db-9d06-bfbd453e25e5"),sQuery(id+"F0.wireOp",EDGE,"E16"),sQuery(id+"F0.wireOp",EDGE,"E17"),sQuery(id+"F0.wireOp",EDGE,"E18"),sQuery(id+"F0.wireOp",EDGE,"E19"),sQuery(id+"F0.wireOp",EDGE,"E20"),sQuery(id+"F0.wireOp",EDGE,"E21"),sQuery(id+"F0.wireOp",EDGE,"E22"),sQuery(id+"F0.wireOp",EDGE,"E23"),sQuery(id+"F0.wireOp",EDGE,"2c05487f-aafa-4f7c-aa8f-dc711a0f5cb2"),sQuery(id+"F0.wireOp",EDGE,"aa923bbd-f832-4f58-9164-6b3256058c8c"),sQuery(id+"F0.wireOp",EDGE,"d95c7900-678d-4411-9ef4-11f17a881cd2"),sQuery(id+"F0.wireOp",EDGE,"E24.filletArc"),sQuery(id+"F0.wireOp",EDGE,"E25.filletArc"),sQuery(id+"F0.wireOp",EDGE,"E26.filletArc"),sQuery(id+"F0.wireOp",EDGE,"E27.filletArc"),sQuery(id+"F0.wireOp",EDGE,"E28"),sQuery(id+"F0.wireOp",EDGE,"E29"),sQuery(id+"F0.wireOp",EDGE,"E30"),sQuery(id+"F0.wireOp",EDGE,"E31"),sQuery(id+"F0.wireOp",EDGE,"E32"),sQuery(id+"F0.wireOp",EDGE,"E33"),sQuery(id+"F0.wireOp",EDGE,"E34"),sQuery(id+"F0.wireOp",EDGE,"E35"),sQuery(id+"F0.wireOp",EDGE,"E36"),sQuery(id+"F0.wireOp",EDGE,"7487c359-1d13-442e-8d40-6b6f0a60b528"),sQuery(id+"F0.wireOp",EDGE,"0d321a95-f0bf-4603-844a-9d89d9bece21"),sQuery(id+"F0.wireOp",EDGE,"0b63d352-fbcd-48db-a107-9c6472e04aa2"),sQuery(id+"F0.wireOp",EDGE,"E37.filletArc"),sQuery(id+"F0.wireOp",EDGE,"E38.filletArc"),sQuery(id+"F0.wireOp",EDGE,"E39.filletArc"),sQuery(id+"F0.wireOp",EDGE,"E40.filletArc"),sQuery(id+"F0.wireOp",EDGE,"67e7e0cc-1dbd-4a8f-987f-19f6fc1f17c7"),sQuery(id+"F0.wireOp",EDGE,"E41"),sQuery(id+"F0.wireOp",EDGE,"E42"),sQuery(id+"F0.wireOp",EDGE,"E43"),sQuery(id+"F0.wireOp",EDGE,"E44"),sQuery(id+"F0.wireOp",EDGE,"E45"),sQuery(id+"F0.wireOp",EDGE,"E46"),sQuery(id+"F0.wireOp",EDGE,"E47"),sQuery(id+"F0.wireOp",EDGE,"E48"),sQuery(id+"F0.wireOp",EDGE,"d55768ac-2e07-4581-96c8-90a235a94c6e"),sQuery(id+"F0.wireOp",EDGE,"d56cd83a-e035-431e-9127-d553bba9e061"),sQuery(id+"F0.wireOp",EDGE,"8d056239-58ce-4037-b7b6-6b57657910ae"),sQuery(id+"F0.wireOp",EDGE,"E49.filletArc"),sQuery(id+"F0.wireOp",EDGE,"E50.filletArc"),sQuery(id+"F0.wireOp",EDGE,"E51.filletArc"),sQuery(id+"F0.wireOp",EDGE,"E52.filletArc"),sQuery(id+"F0.wireOp",EDGE,"689b71ce-addc-4fa1-bc7e-e4df8c8ebdf9"),sQuery(id+"F0.wireOp",EDGE,"E53"),sQuery(id+"F0.wireOp",EDGE,"E54"),sQuery(id+"F0.wireOp",EDGE,"E55"),sQuery(id+"F0.wireOp",EDGE,"E56"),sQuery(id+"F0.wireOp",EDGE,"E57"),sQuery(id+"F0.wireOp",EDGE,"E58"),sQuery(id+"F0.wireOp",EDGE,"E59"),sQuery(id+"F0.wireOp",EDGE,"E60"),sQuery(id+"F0.wireOp",EDGE,"0f5e8a53-58f9-4088-94ab-621361dd0740"),sQuery(id+"F0.wireOp",EDGE,"c80b85d9-e73a-4eb2-b9b9-34d3dfa9f6f2"),sQuery(id+"F0.wireOp",EDGE,"70b4659f-ba04-44f8-9531-555b2133b5da"),sQuery(id+"F0.wireOp",EDGE,"E61.filletArc"),sQuery(id+"F0.wireOp",EDGE,"E62.filletArc"),sQuery(id+"F0.wireOp",EDGE,"E63.filletArc"),sQuery(id+"F0.wireOp",EDGE,"E64.filletArc"),sQuery(id+"F0.wireOp",EDGE,"30e6c9bc-ddc1-4fb0-937a-8d0deabf5910"),sQuery(id+"F0.wireOp",EDGE,"E65"),sQuery(id+"F0.wireOp",EDGE,"E66"),sQuery(id+"F0.wireOp",EDGE,"E67"),sQuery(id+"F0.wireOp",EDGE,"E68"),sQuery(id+"F0.wireOp",EDGE,"E69"),sQuery(id+"F0.wireOp",EDGE,"E70"),sQuery(id+"F0.wireOp",EDGE,"E71"),sQuery(id+"F0.wireOp",EDGE,"E72"),sQuery(id+"F0.wireOp",EDGE,"8f9fa5c3-c251-432c-b5cf-c271094e8503"),sQuery(id+"F0.wireOp",EDGE,"48fe9f69-4303-4a16-b855-5b18747e6bbd"),sQuery(id+"F0.wireOp",EDGE,"adddb319-75e6-4134-aa0c-543cc49d29cf"),sQuery(id+"F0.wireOp",EDGE,"E73.filletArc"),sQuery(id+"F0.wireOp",EDGE,"E74.filletArc"),sQuery(id+"F0.wireOp",EDGE,"E75.filletArc"),sQuery(id+"F0.wireOp",EDGE,"E76.filletArc"),sQuery(id+"F0.wireOp",EDGE,"794929a8-fd93-45ab-9b8a-a8aae1a8e309"),sQuery(id+"F0.wireOp",EDGE,"E77"),sQuery(id+"F0.wireOp",EDGE,"E78"),sQuery(id+"F0.wireOp",EDGE,"E79"),sQuery(id+"F0.wireOp",EDGE,"E80"),sQuery(id+"F0.wireOp",EDGE,"E81"),sQuery(id+"F0.wireOp",EDGE,"E82"),sQuery(id+"F0.wireOp",EDGE,"E83"),sQuery(id+"F0.wireOp",EDGE,"E84"),sQuery(id+"F0.wireOp",EDGE,"c2507384-40c0-4369-9541-7014aa20dc06"),sQuery(id+"F0.wireOp",EDGE,"1daf244b-b26d-4da6-aa17-2b1b48277eff"),sQuery(id+"F0.wireOp",EDGE,"f3f5064b-9514-43f3-86fe-7d8dfe96d7c0"),sQuery(id+"F0.wireOp",EDGE,"E85.filletArc"),sQuery(id+"F0.wireOp",EDGE,"E86.filletArc"),sQuery(id+"F0.wireOp",EDGE,"E87.filletArc"),sQuery(id+"F0.wireOp",EDGE,"E88.filletArc"),sQuery(id+"F0.wireOp",EDGE,"db05fb30-ff1c-46d8-ad61-f310132a52e9"),sQuery(id+"F0.wireOp",EDGE,"E89"),sQuery(id+"F0.wireOp",EDGE,"E90"),sQuery(id+"F0.wireOp",EDGE,"E91"),sQuery(id+"F0.wireOp",EDGE,"E92"),sQuery(id+"F0.wireOp",EDGE,"E93"),sQuery(id+"F0.wireOp",EDGE,"E94"),sQuery(id+"F0.wireOp",EDGE,"E95"),sQuery(id+"F0.wireOp",EDGE,"E96"),sQuery(id+"F0.wireOp",EDGE,"1130a4e5-352a-40db-811d-9c2f480c6459"),sQuery(id+"F0.wireOp",EDGE,"eab22e00-a051-4c91-887e-3bb937c10980"),sQuery(id+"F0.wireOp",EDGE,"d1e682f2-d9a5-40f1-908d-0a2fb979e1ca"),sQuery(id+"F0.wireOp",EDGE,"E97.filletArc"),sQuery(id+"F0.wireOp",EDGE,"E98.filletArc"),sQuery(id+"F0.wireOp",EDGE,"E99.filletArc"),sQuery(id+"F0.wireOp",EDGE,"E100.filletArc"),sQuery(id+"F0.wireOp",EDGE,"e89af864-c7d1-4349-afac-df63decef93c"),sQuery(id+"F0.wireOp",EDGE,"E101"),sQuery(id+"F0.wireOp",EDGE,"E102"),sQuery(id+"F0.wireOp",EDGE,"E103"),sQuery(id+"F0.wireOp",EDGE,"E104"),sQuery(id+"F0.wireOp",EDGE,"E105"),sQuery(id+"F0.wireOp",EDGE,"E106"),sQuery(id+"F0.wireOp",EDGE,"E107"),sQuery(id+"F0.wireOp",EDGE,"E108"),sQuery(id+"F0.wireOp",EDGE,"23fffc08-2727-465d-9e6f-753851ddf39a"),sQuery(id+"F0.wireOp",EDGE,"E109"),sQuery(id+"F0.wireOp",EDGE,"E110"),sQuery(id+"F0.wireOp",EDGE,"E111.filletArc"),sQuery(id+"F0.wireOp",EDGE,"E112.filletArc"),sQuery(id+"F0.wireOp",EDGE,"E113.filletArc"),sQuery(id+"F0.wireOp",EDGE,"E114.filletArc"),sQuery(id+"F0.wireOp",EDGE,"E115"),sQuery(id+"F0.wireOp",EDGE,"E116"),sQuery(id+"F0.wireOp",EDGE,"E117"),sQuery(id+"F0.wireOp",EDGE,"E118")])]});
            transform(context, id + "F7", {"entities" : qUnion([Q0]), "transformType" : TransformType.TRANSLATION_3D, "dx" : 70.87 * mm, "dy" : 0 * mm, "dz" : 0 * mm, "makeCopy" : false});
        }
    });
